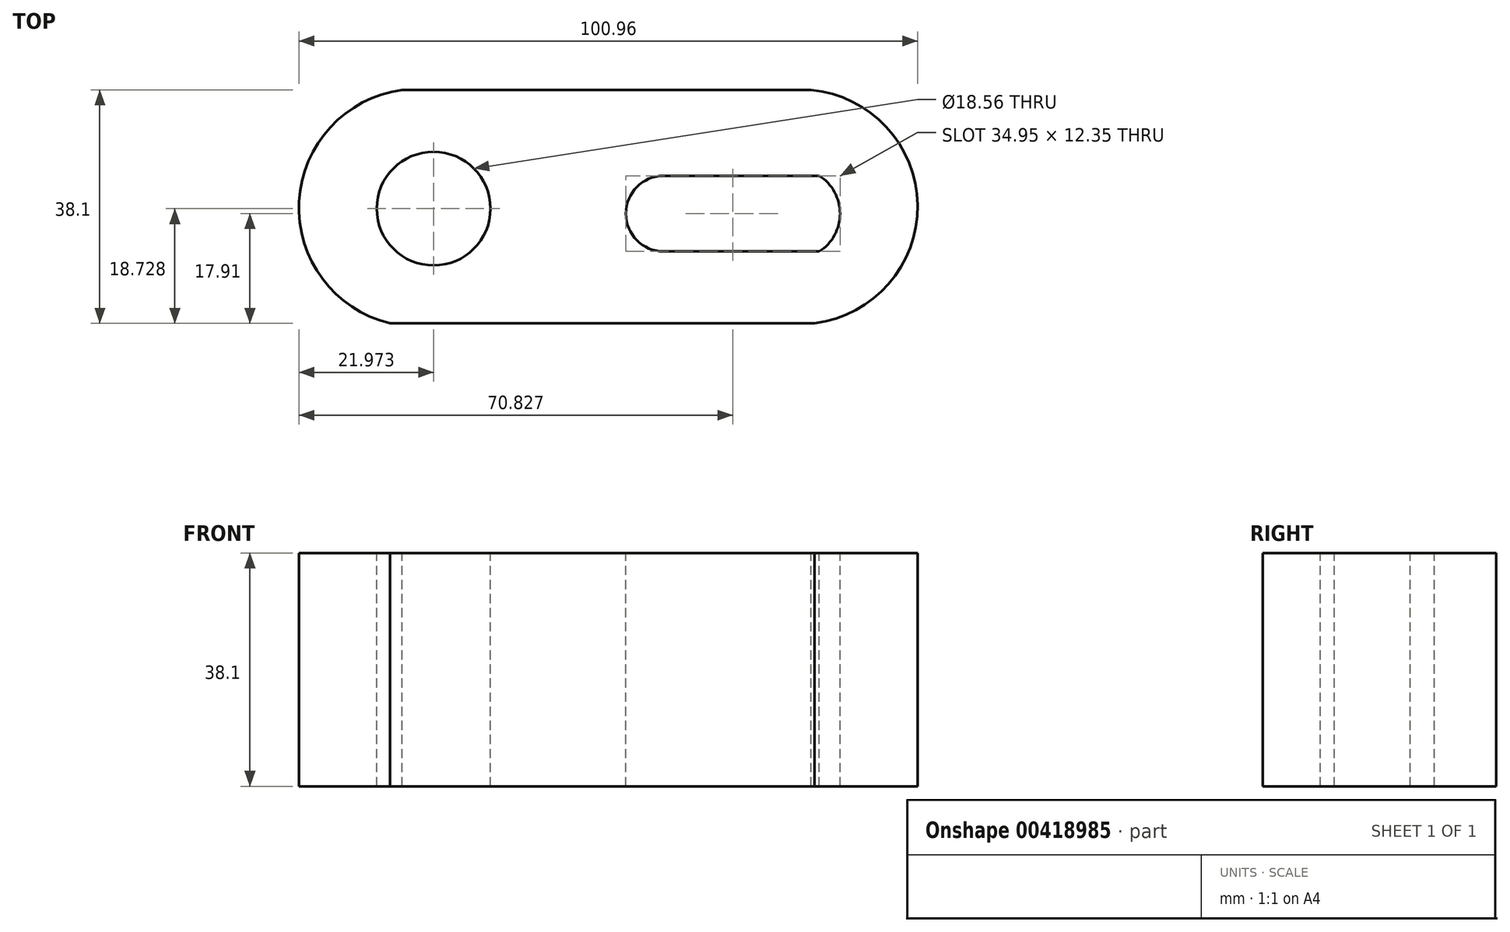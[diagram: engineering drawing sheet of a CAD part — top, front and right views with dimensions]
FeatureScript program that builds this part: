
annotation { "Feature Type Name" : "Feature", "Feature Type Description" : "" }
export const myFeature = defineFeature(function(context is Context, id is Id, definition is map)
    precondition{}
    {
        {
            var Q0;
            Q0=qCreatedBy(makeId("Front.planeOp"),FACE);
            var sketch = newSketch(context, id + "F0", { "sketchPlane" : qUnion([Q0])});
            skLineSegment(sketch, "E0.bottom", {"start": v(0, 0) * mm, "end": v(101.6, 0) * mm});
            skLineSegment(sketch, "E0.top", {"start": v(0, 38.1) * mm, "end": v(101.6, 38.1) * mm});
            skLineSegment(sketch, "E0.left", {"start": v(0, 0) * mm, "end": v(0, 38.1) * mm});
            skLineSegment(sketch, "E0.right", {"start": v(101.6, 0) * mm, "end": v(101.6, 38.1) * mm});
            skSolve(sketch);
        }
        {
            var Q0;
            Q0=makeQuery(id+"F0.imprint","IMPRINT",FACE,{"disambiguationData":[TD([[makeQuery(id+"F0.imprint","IMPRINT",EDGE,{"derivedFrom":sQuery(id+"F0.wireOp",EDGE,"E0.bottom")}),1.0]])]});
            extrude(context, id + "F1", {"entities" : qUnion([Q0]), "depth" : 38.1 * mm});
        }
        {
            var Q0;
            Q0=makeQuery(id+"F1.opExtrude","SWEPT_FACE",FACE,{"disambiguationData":[OSD([sQuery(id+"F0.wireOp",EDGE,"E0.top")])]});
            var sketch = newSketch(context, id + "F2", { "sketchPlane" : qUnion([Q0])});
            skArc(sketch, "E1", {"start": v(84.48, -38.1) * mm, "mid": v(101.33, -18.8) * mm, "end": v(83.91, 0) * mm});
            skArc(sketch, "E2", {"start": v(22.35, 0) * mm, "mid": v(0.4, -20.25) * mm, "end": v(24.33, -38.1) * mm});
            skSolve(sketch);
        }
        {
            var Q0;
            Q0 = qSketchRegion(id + "F2", true);
            var Q1;
            {var subQ0=sQuery(id+"F2.wireOp",EDGE,"E1");Q1=makeQuery(id+"F2.imprint","IMPRINT",FACE,{"disambiguationData":[TD([[makeQuery(id+"F2.imprint","IMPRINT",EDGE,{"derivedFrom":subQ0}),-1.0]])]});}
            var Q2;
            {var subQ1=sQuery(id+"F0.wireOp",EDGE,"E0.top");var subQ6=makeQuery(id+"F1.opExtrude","SWEPT_EDGE",EDGE,{"disambiguationData":[OSD([subQ1,sQuery(id+"F0.wireOp",EDGE,"E0.left")])]});Q2=makeQuery(id+"F2.imprint","IMPRINT",FACE,{"disambiguationData":[TD([[makeQuery(id+"F2.imprint","IMPRINT",EDGE,{"derivedFrom":subQ6}),-1.0]])]});}
            extrude(context, id + "F3", {"entities" : qUnion([Q0, Q1, Q2]), "operationType" : NewBodyOperationType.REMOVE, "oppositeDirection" : true, "depth" : 38.1 * mm});
        }
        {
            var Q0;
            Q0=makeQuery(id+"F1.opExtrude","SWEPT_FACE",FACE,{"disambiguationData":[OSD([sQuery(id+"F0.wireOp",EDGE,"E0.top")])]});
            var sketch = newSketch(context, id + "F4", { "sketchPlane" : qUnion([Q0])});
            skCircle(sketch, "E3", {"center": v(22.34, -19.37) * mm, "radius": 9.28 * mm});
            skSolve(sketch);
        }
        {
            var Q0;
            Q0=makeQuery(id+"F4.imprint","IMPRINT",FACE,{"disambiguationData":[TD([[makeQuery(id+"F4.imprint","IMPRINT",EDGE,{"derivedFrom":sQuery(id+"F4.wireOp",EDGE,"E3")}),1.0]])]});
            extrude(context, id + "F5", {"entities" : qUnion([Q0]), "operationType" : NewBodyOperationType.REMOVE, "oppositeDirection" : true, "depth" : 38.1 * mm});
        }
        {
            var Q0;
            Q0=makeQuery(id+"F1.opExtrude","SWEPT_FACE",FACE,{"disambiguationData":[OSD([sQuery(id+"F0.wireOp",EDGE,"E0.top")])]});
            var sketch = newSketch(context, id + "F6", { "sketchPlane" : qUnion([Q0])});
            skLineSegment(sketch, "E4", {"start": v(59.9, -14.02) * mm, "end": v(85.3, -14.02) * mm});
            skLineSegment(sketch, "E5", {"start": v(59.9, -26.36) * mm, "end": v(85.3, -26.36) * mm});
            skArc(sketch, "E6", {"start": v(59.9, -14.02) * mm, "mid": v(53.72, -20.19) * mm, "end": v(59.9, -26.36) * mm});
            skArc(sketch, "E7", {"start": v(85.3, -26.36) * mm, "mid": v(88.67, -20.19) * mm, "end": v(85.3, -14.02) * mm});
            skSolve(sketch);
        }
        {
            var Q0;
            Q0=makeQuery(id+"F6.imprint","IMPRINT",FACE,{"disambiguationData":[TD([[makeQuery(id+"F6.imprint","IMPRINT",EDGE,{"derivedFrom":sQuery(id+"F6.wireOp",EDGE,"E4")}),-1.0]])]});
            extrude(context, id + "F7", {"entities" : qUnion([Q0]), "operationType" : NewBodyOperationType.REMOVE, "oppositeDirection" : true, "depth" : 101.6 * mm});
        }
    });
